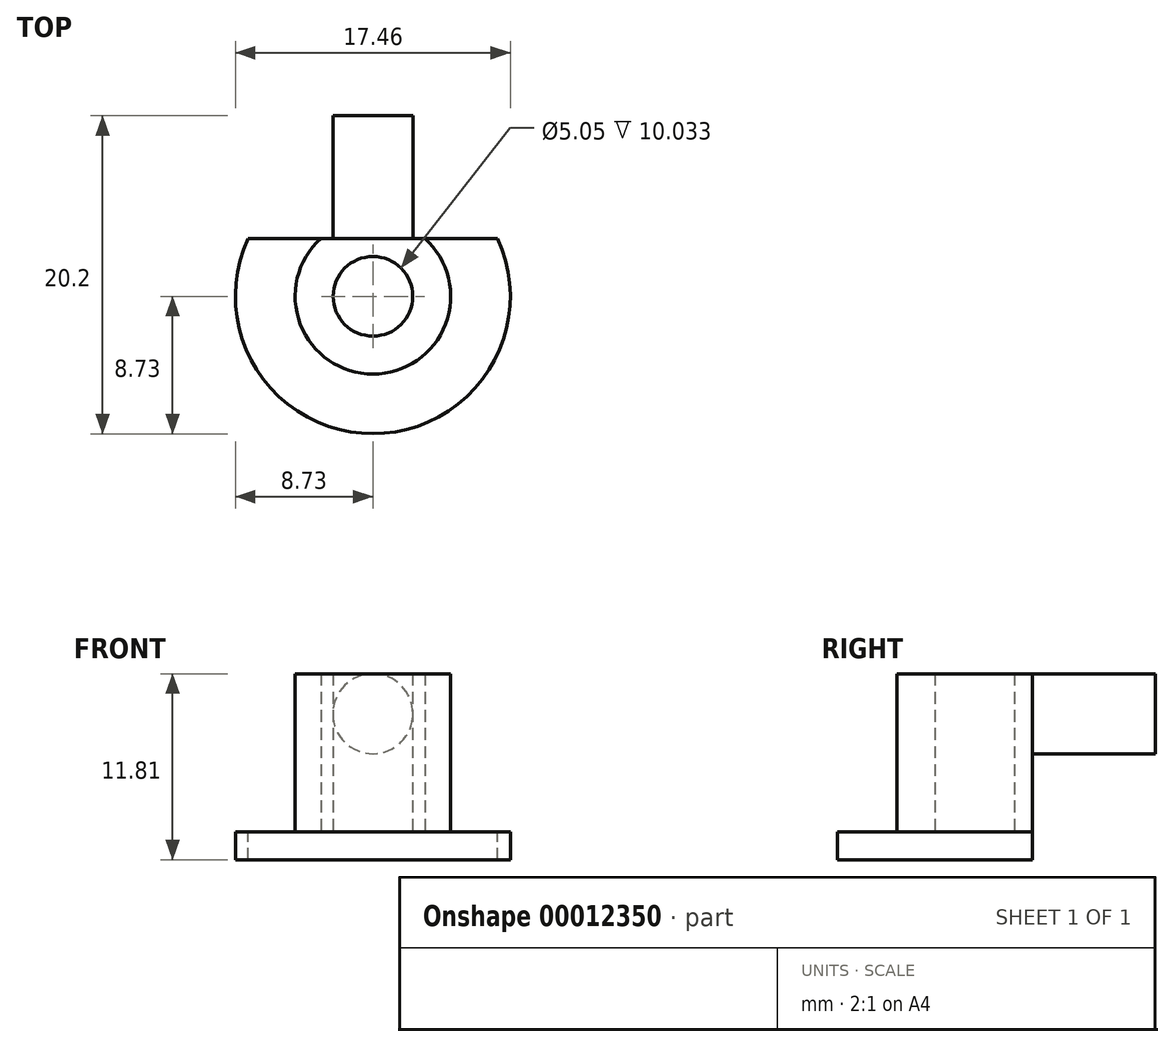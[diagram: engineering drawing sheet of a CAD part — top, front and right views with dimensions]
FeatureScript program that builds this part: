
annotation { "Feature Type Name" : "Feature", "Feature Type Description" : "" }
export const myFeature = defineFeature(function(context is Context, id is Id, definition is map)
    precondition{}
    {
        {
            var Q0;
            Q0=qCreatedBy(makeId("Top.planeOp"),FACE);
            var sketch = newSketch(context, id + "F0", { "sketchPlane" : qUnion([Q0])});
            skArc(sketch, "E0", {"start": v(-3.3, 3.67) * mm, "mid": v(0, -4.94) * mm, "end": v(3.3, 3.67) * mm});
            skCircle(sketch, "E1", {"center": v(0, 0) * mm, "radius": 2.53 * mm});
            skLineSegment(sketch, "E2", {"start": v(0, 3.67) * mm, "end": v(-3.3, 3.67) * mm});
            skLineSegment(sketch, "E3", {"start": v(-3.3, 3.67) * mm, "end": v(0, 3.67) * mm});
            skLineSegment(sketch, "E4", {"start": v(0, 3.67) * mm, "end": v(3.3, 3.67) * mm});
            skSolve(sketch);
        }
        {
            var Q0;
            Q0=makeQuery(id+"F0.imprint","IMPRINT",FACE,{"disambiguationData":[TD([[makeQuery(id+"F0.imprint","IMPRINT",EDGE,{"derivedFrom":sQuery(id+"F0.wireOp",EDGE,"E0")}),1.0]])]});
            extrude(context, id + "F1", {"entities" : qUnion([Q0]), "depth" : 10.03 * mm});
        }
        {
            var Q0;
            Q0=makeQuery(id+"F0.imprint","IMPRINT",FACE,{"disambiguationData":[TD([[makeQuery(id+"F0.imprint","IMPRINT",EDGE,{"derivedFrom":sQuery(id+"F0.wireOp",EDGE,"E0")}),1.0]])]});
            var sketch = newSketch(context, id + "F2", { "sketchPlane" : qUnion([Q0])});
            skCircle(sketch, "E5", {"center": v(0, 0) * mm, "radius": 8.73 * mm});
            skLineSegment(sketch, "E6", {"start": v(-7.92, 3.67) * mm, "end": v(7.92, 3.67) * mm});
            skSolve(sketch);
        }
        {
            var Q0;
            Q0=makeQuery(id+"F2.imprint","IMPRINT",FACE,{"disambiguationData":[TD([[makeQuery(id+"F2.imprint","IMPRINT",EDGE,{"derivedFrom":makeQuery(id+"F0.imprint","IMPRINT",EDGE,{"derivedFrom":sQuery(id+"F0.wireOp",EDGE,"E1")})}),1.0]])]});
            var Q1;
            Q1=makeQuery(id+"F2.imprint","IMPRINT",FACE,{"disambiguationData":[TD([[makeQuery(id+"F2.imprint","IMPRINT",EDGE,{"derivedFrom":makeQuery(id+"F0.imprint","IMPRINT",EDGE,{"derivedFrom":sQuery(id+"F0.wireOp",EDGE,"E0")})}),1.0]])]});
            var Q2;
            Q2=makeQuery(id+"F2.imprint","IMPRINT",FACE,{"disambiguationData":[TD([[makeQuery(id+"F2.imprint","IMPRINT",EDGE,{"derivedFrom":sQuery(id+"F2.wireOp",EDGE,"E5")}),1.0]])]});
            extrude(context, id + "F3", {"entities" : qUnion([Q0, Q1, Q2]), "operationType" : NewBodyOperationType.ADD, "oppositeDirection" : true, "depth" : 1.78 * mm});
        }
        {
            var Q0;
            Q0=makeQuery(id+"F1.opExtrude","SWEPT_FACE",FACE,{"disambiguationData":[OSD([sQuery(id+"F0.wireOp",EDGE,"E3"),sQuery(id+"F0.wireOp",EDGE,"E4")])]});
            var sketch = newSketch(context, id + "F4", { "sketchPlane" : qUnion([Q0])});
            skCircle(sketch, "E7", {"center": v(0, 7.5) * mm, "radius": 2.54 * mm});
            skSolve(sketch);
        }
        {
            var Q0;
            Q0=makeQuery(id+"F4.imprint","IMPRINT",FACE,{"disambiguationData":[TD([[makeQuery(id+"F4.imprint","IMPRINT",EDGE,{"derivedFrom":sQuery(id+"F4.wireOp",EDGE,"E7")}),1.0]])]});
            extrude(context, id + "F5", {"entities" : qUnion([Q0]), "operationType" : NewBodyOperationType.ADD, "depth" : 7.8 * mm});
        }
    });
